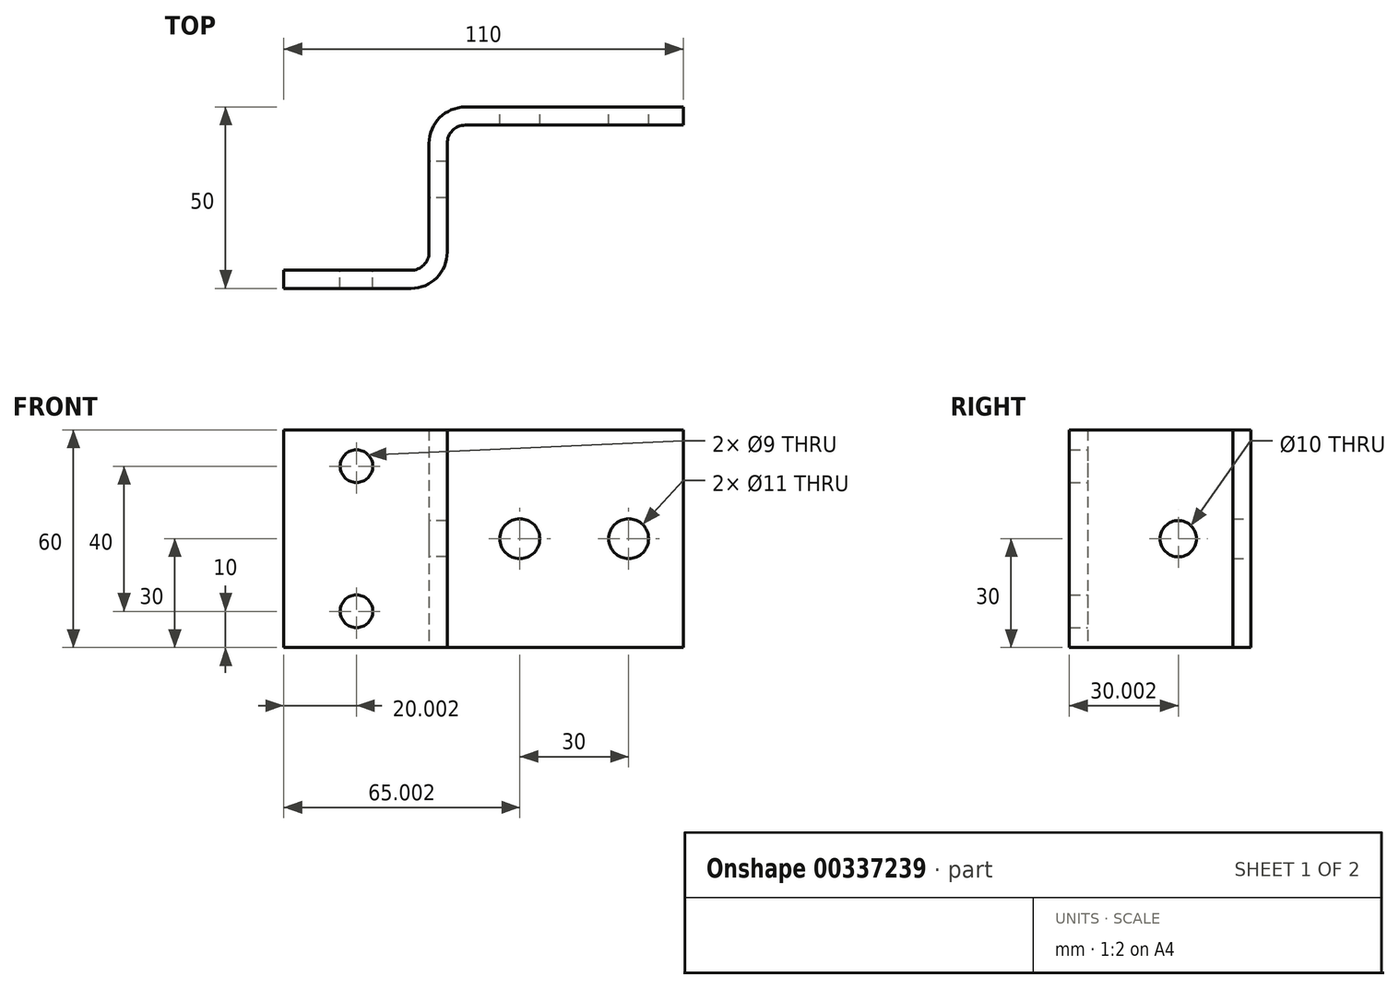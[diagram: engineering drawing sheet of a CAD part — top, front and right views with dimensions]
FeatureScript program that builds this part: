
annotation { "Feature Type Name" : "Feature", "Feature Type Description" : "" }
export const myFeature = defineFeature(function(context is Context, id is Id, definition is map)
    precondition{}
    {
        {
            var Q0;
            Q0=qCreatedBy(makeId("Top.planeOp"),FACE);
            var sketch = newSketch(context, id + "F0", { "sketchPlane" : qUnion([Q0])});
            skLineSegment(sketch, "E0", {"start": v(-51.96, -29.14) * mm, "end": v(-16.96, -29.14) * mm});
            skLineSegment(sketch, "E1", {"start": v(-11.96, -24.14) * mm, "end": v(-11.96, 5.86) * mm});
            skLineSegment(sketch, "E2", {"start": v(-1.96, 15.86) * mm, "end": v(58.04, 15.86) * mm});
            skLineSegment(sketch, "E3", {"start": v(58.04, 15.86) * mm, "end": v(58.04, 10.86) * mm});
            skLineSegment(sketch, "E4", {"start": v(58.04, 10.86) * mm, "end": v(-1.96, 10.86) * mm});
            skLineSegment(sketch, "E5", {"start": v(-6.96, 5.86) * mm, "end": v(-6.96, -24.14) * mm});
            skLineSegment(sketch, "E6", {"start": v(-16.96, -34.14) * mm, "end": v(-51.96, -34.14) * mm});
            skLineSegment(sketch, "E7", {"start": v(-51.96, -34.14) * mm, "end": v(-51.96, -29.14) * mm});
            skPoint(sketch, "E8.visualSharp", {"position": v(-11.96, -29.14) * mm});
            skArc(sketch, "E8.filletArc", {"start": v(-16.96, -29.14) * mm, "mid": v(-13.42, -27.67) * mm, "end": v(-11.96, -24.14) * mm});
            skPoint(sketch, "E9.visualSharp", {"position": v(-6.96, 10.86) * mm});
            skArc(sketch, "E9.filletArc", {"start": v(-1.96, 10.86) * mm, "mid": v(-5.5, 9.4) * mm, "end": v(-6.96, 5.86) * mm});
            skPoint(sketch, "E10.visualSharp", {"position": v(-11.96, 15.86) * mm});
            skArc(sketch, "E10.filletArc", {"start": v(-1.96, 15.86) * mm, "mid": v(-9.03, 12.93) * mm, "end": v(-11.96, 5.86) * mm});
            skPoint(sketch, "E11.visualSharp", {"position": v(-6.96, -34.14) * mm});
            skArc(sketch, "E11.filletArc", {"start": v(-16.96, -34.14) * mm, "mid": v(-9.89, -31.2) * mm, "end": v(-6.96, -24.14) * mm});
            skSolve(sketch);
        }
        {
            var Q0;
            Q0 = qSketchRegion(id + "F0", true);
            extrude(context, id + "F1", {"entities" : qUnion([Q0]), "depth" : 60 * mm});
        }
        {
            var Q0;
            Q0 = qSketchRegion(id + "F0", true);
            extrude(context, id + "F2", {"entities" : qUnion([Q0]), "operationType" : NewBodyOperationType.ADD, "depth" : 60 * mm});
        }
        {
            var Q0;
            Q0=makeQuery(id+"F1.opExtrude","SWEPT_FACE",FACE,{"disambiguationData":[OSD([sQuery(id+"F0.wireOp",EDGE,"E0")])]});
            var sketch = newSketch(context, id + "F3", { "sketchPlane" : qUnion([Q0])});
            skPoint(sketch, "E12.end.orphan", {"position": v(31.96, 0) * mm});
            skPoint(sketch, "E13.end.orphan", {"position": v(31.96, 10) * mm});
            skCircle(sketch, "E14", {"center": v(31.96, 10) * mm, "radius": 4.5 * mm});
            skCircle(sketch, "E15", {"center": v(31.96, 50) * mm, "radius": 4.5 * mm});
            skPoint(sketch, "E16.orphan", {"position": v(31.96, 60) * mm});
            skCircle(sketch, "E17", {"center": v(-13.04, 30) * mm, "radius": 5.5 * mm});
            skCircle(sketch, "E18", {"center": v(-42.59, 30) * mm, "radius": 5.5 * mm});
            skSolve(sketch);
        }
        {
            var Q0;
            Q0=makeQuery(id+"F3.imprint","IMPRINT",FACE,{"disambiguationData":[TD([[makeQuery(id+"F3.imprint","IMPRINT",EDGE,{"derivedFrom":sQuery(id+"F3.wireOp",EDGE,"E14")}),1.0]])]});
            var Q1;
            Q1=makeQuery(id+"F3.imprint","IMPRINT",FACE,{"disambiguationData":[TD([[makeQuery(id+"F3.imprint","IMPRINT",EDGE,{"derivedFrom":sQuery(id+"F3.wireOp",EDGE,"E15")}),1.0]])]});
            extrude(context, id + "F4", {"entities" : qUnion([Q0, Q1]), "operationType" : NewBodyOperationType.REMOVE, "oppositeDirection" : true, "depth" : 25 * mm});
        }
        {
            var Q0;
            Q0=makeQuery(id+"F1.opExtrude","SWEPT_FACE",FACE,{"disambiguationData":[OSD([sQuery(id+"F0.wireOp",EDGE,"E2")])]});
            var sketch = newSketch(context, id + "F5", { "sketchPlane" : qUnion([Q0])});
            skCircle(sketch, "E19", {"center": v(-43.04, 30) * mm, "radius": 5.5 * mm});
            skCircle(sketch, "E20", {"center": v(-13.04, 30) * mm, "radius": 5.5 * mm});
            skSolve(sketch);
        }
        {
            var Q0;
            Q0=makeQuery(id+"F5.imprint","IMPRINT",FACE,{"disambiguationData":[TD([[makeQuery(id+"F5.imprint","IMPRINT",EDGE,{"derivedFrom":sQuery(id+"F5.wireOp",EDGE,"E20")}),1.0]])]});
            var Q1;
            Q1=makeQuery(id+"F5.imprint","IMPRINT",FACE,{"disambiguationData":[TD([[makeQuery(id+"F5.imprint","IMPRINT",EDGE,{"derivedFrom":sQuery(id+"F5.wireOp",EDGE,"E19")}),1.0]])]});
            extrude(context, id + "F6", {"entities" : qUnion([Q0, Q1]), "operationType" : NewBodyOperationType.REMOVE, "oppositeDirection" : true, "depth" : 25 * mm});
        }
        {
            var Q0;
            Q0=makeQuery(id+"F1.opExtrude","SWEPT_FACE",FACE,{"disambiguationData":[OSD([sQuery(id+"F0.wireOp",EDGE,"E1")])]});
            var sketch = newSketch(context, id + "F7", { "sketchPlane" : qUnion([Q0])});
            skCircle(sketch, "E21", {"center": v(4.14, 30) * mm, "radius": 5 * mm});
            skPoint(sketch, "E22.orphan", {"position": v(-5.86, 30) * mm});
            skPoint(sketch, "E23.end.orphan", {"position": v(-5.86, 29.64) * mm});
            skSolve(sketch);
        }
        {
            var Q0;
            Q0=makeQuery(id+"F7.imprint","IMPRINT",FACE,{"disambiguationData":[TD([[makeQuery(id+"F7.imprint","IMPRINT",EDGE,{"derivedFrom":sQuery(id+"F7.wireOp",EDGE,"E21")}),1.0]])]});
            extrude(context, id + "F8", {"entities" : qUnion([Q0]), "operationType" : NewBodyOperationType.REMOVE, "oppositeDirection" : true, "depth" : 25 * mm});
        }
        {
            var Q0;
            Q0=makeQuery(id+"F7.imprint","IMPRINT",FACE,{"disambiguationData":[TD([[makeQuery(id+"F7.imprint","IMPRINT",EDGE,{"derivedFrom":sQuery(id+"F7.wireOp",EDGE,"E21")}),1.0]])]});
            extrude(context, id + "F9", {"entities" : qUnion([Q0]), "operationType" : NewBodyOperationType.REMOVE, "oppositeDirection" : true, "depth" : 25 * mm});
        }
        {
            var Q0;
            Q0=makeQuery(id+"F7.imprint","IMPRINT",FACE,{"disambiguationData":[TD([[makeQuery(id+"F7.imprint","IMPRINT",EDGE,{"derivedFrom":sQuery(id+"F7.wireOp",EDGE,"E21")}),1.0]])]});
            extrude(context, id + "F10", {"entities" : qUnion([Q0]), "operationType" : NewBodyOperationType.REMOVE, "oppositeDirection" : true, "depth" : 25 * mm});
        }
        {
            var Q0;
            Q0 = qSketchRegion(id + "F7", true);
            extrude(context, id + "F11", {"entities" : qUnion([Q0]), "operationType" : NewBodyOperationType.REMOVE, "oppositeDirection" : true, "depth" : 25 * mm});
        }
    });
